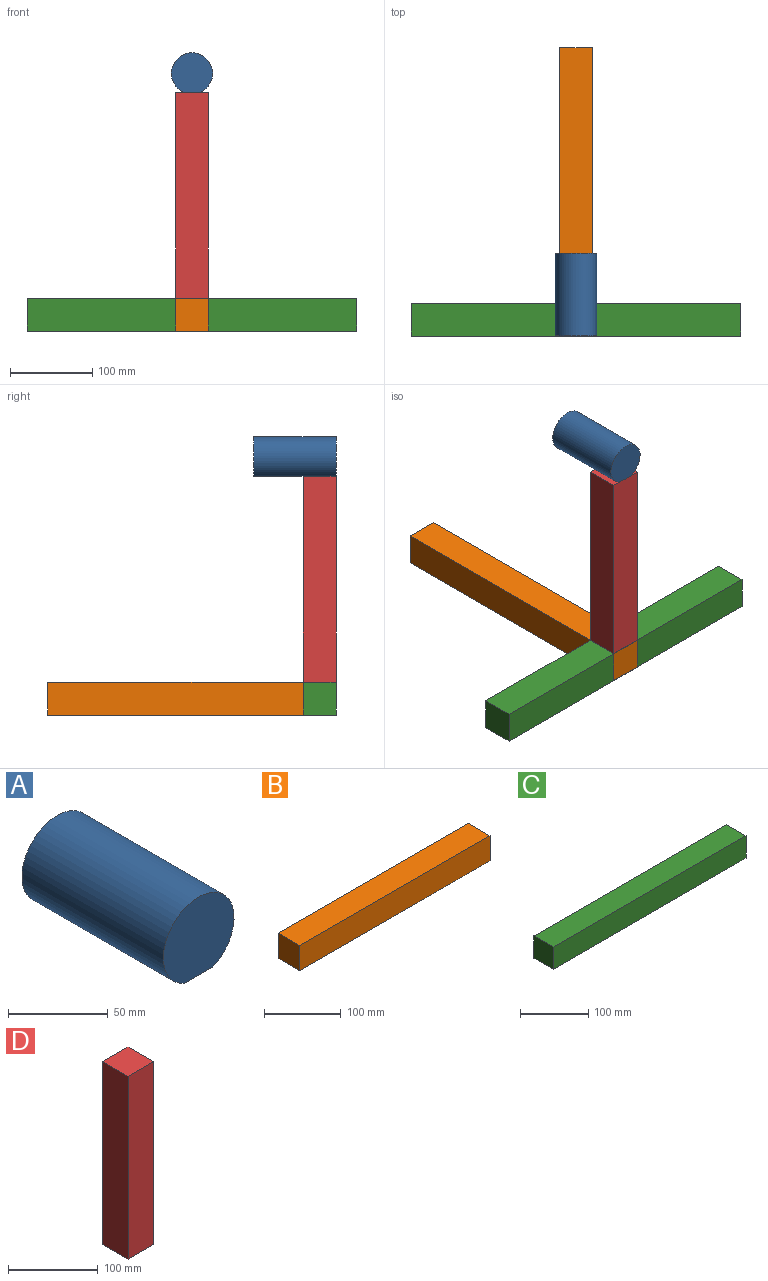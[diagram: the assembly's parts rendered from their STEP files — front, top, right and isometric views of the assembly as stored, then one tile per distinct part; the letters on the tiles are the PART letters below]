
ASSEMBLY  parts=4 mates=3
PART A: 4 faces, bbox 50x100x47.9 mm
  f0: cylinder r=25mm len=100mm, axis (0,1,0), area 13650.4mm2, adj f1,f2,f3
  f1: plane 100x20mm, normal (0,0,-1), area 2000mm2, adj f0,f2,f3
  f2: plane 50x47.91mm, normal (0,-1,0), area 1935.4mm2, adj f0,f1
  f3: plane 50x47.91mm, normal (0,1,0), area 1935.4mm2, adj f0,f1
PART B: 6 faces, bbox 350x40x40 mm
  f0: plane 350x40mm, normal (0,0,1), area 14000mm2, adj f1,f3,f4,f5
  f1: plane 40x40mm, normal (-1,0,0), area 1600mm2, adj f0,f2,f4,f5
  f2: plane 350x40mm, normal (0,0,-1), area 14000mm2, adj f1,f3,f4,f5
  f3: plane 40x40mm, normal (1,0,0), area 1600mm2, adj f0,f2,f4,f5
  f4: plane 350x40mm, normal (0,-1,0), area 14000mm2, adj f0,f1,f2,f3
  f5: plane 350x40mm, normal (0,1,0), area 14000mm2, adj f0,f1,f2,f3
PART C: 6 faces, bbox 400x40x40 mm
  f0: plane 400x40mm, normal (0,0,1), area 16000mm2, adj f1,f3,f4,f5
  f1: plane 40x40mm, normal (-1,0,0), area 1600mm2, adj f0,f2,f4,f5
  f2: plane 400x40mm, normal (0,0,-1), area 16000mm2, adj f1,f3,f4,f5
  f3: plane 40x40mm, normal (1,0,0), area 1600mm2, adj f0,f2,f4,f5
  f4: plane 400x40mm, normal (0,-1,0), area 16000mm2, adj f0,f1,f2,f3
  f5: plane 400x40mm, normal (0,1,0), area 16000mm2, adj f0,f1,f2,f3
PART D: 6 faces, bbox 40x40x250 mm
  f0: plane 40x40mm, normal (0,0,1), area 1600mm2, adj f1,f3,f4,f5
  f1: plane 250x40mm, normal (-1,0,0), area 10000mm2, adj f0,f2,f4,f5
  f2: plane 40x40mm, normal (0,0,-1), area 1600mm2, adj f1,f3,f4,f5
  f3: plane 250x40mm, normal (1,0,0), area 10000mm2, adj f0,f2,f4,f5
  f4: plane 250x40mm, normal (0,-1,0), area 10000mm2, adj f0,f1,f2,f3
  f5: plane 250x40mm, normal (0,1,0), area 10000mm2, adj f0,f1,f2,f3
PLACE A t=(3.01,72.36,274.02)mm
PLACE B rot(axis=(0.58,-0.58,-0.58),120deg) t=(-2.04,275.96,8.29)mm
PLACE C t=(-13.02,12.36,80.84)mm
PLACE D t=(4.57,12.36,35.98)mm
MATE fastened D.f2 <-> C.f0  axis (0,0,-1) through (0.29,-7.64,8.29)mm
MATE fastened B.f3 <-> C.f4  axis (0,-1,0) through (0.29,-27.64,-11.71)mm
MATE fastened A.f1 <-> D.f0  axis (0,0,-1) through (0.29,-27.64,258.29)mm
